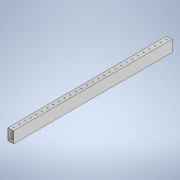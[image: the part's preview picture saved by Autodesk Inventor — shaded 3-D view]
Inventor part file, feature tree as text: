
AUTODESK INVENTOR PART (.ipt)
format: ipt  version: 2020 (Build 240168000, 168)  size: 183,808 bytes
history: native  units: in
note: dims shown in document units (in); Inventor stores cm internally (conversion verified against a paired STEP export)
features: extrude x2, sketch x2
ambient origin geometry x8: Origin, YZ Plane, XZ Plane, XY Plane, X Axis, Y Axis, Z Axis, Center Point
bodies: Solid1 (feature_tree)
feature tree (4):
  extrude  "Extrusion1"  Depth=2.0in
  extrude  "Extrusion2"  Depth=28.0in TaperAngle=0.0deg
  sketch  "Sketch1"  dims[d0=1.0in d1=2.0in]
  sketch  "Sketch2"  dims[d2=0.1in d3=28.0in d4=0.0in d5=0.1562in d6=0.5in d7=0.5in d8=11.4173in d10=1.0in d11=0.3937in d13=1.0in d15=3.0in d16=0.0in]
